# Revit family: Shower-Rainhead-KOHLER-K-26291IN
name_source: partatom
category: Plumbing Fixtures
revit_build: Autodesk Revit 2017 (Build: 20160225_1515(x64)
units: mm (PartAtom-declared; Revit-internal decimal feet)

## family parameters
Cut with Voids When Loaded = No
Host = Face
OmniClass Number = 23.31.17.00
Part Type = Normal
Room Calculation Point = No
Round Connector Dimension = Use Diameter
Shared = No

## types (6) — shared parameters
ADA Compliant = No
Assembly Code = D2010700
CW Connection = No
Cold Water Inlet = Cold Water Inlet
Date Modified = 02/01/2021
Default Elevation = 0"
Description = 10 in Round Katalyst Rainhead 2.5 GPM
Drain Included = No
Flow Rate = 3 GPM
HW Connection = Yes
Height = 4"
Hot Water Inlet = Tempered Water Inlet
Length = 11 15/16"
Manufacturer = KOHLER Co.
Master Format 2014 = 22 42 23
Master Format 2014 Name = Residential Showers
Material = Brass Construction
Pressure = 0.00 psi
URL = https://www.kohler.co.in
Vent Connection = No
Waste Connection = No
Waste Water Outlet = Waste Water Outlet
WaterSense Certified = No
Width = 11 15/16"

## per-type parameters (varying)
| type | Finish | Model | Product Name | Type |
| CP-Polished Chrome | Kohler-Metal-CP-Polished_Chrome | K-26291IN-CP |  | 1 |
| BN-Vibrant Brushed Nickel | Kohler-Metal-BN-Vibrant_Brushed_Nickel | K-26291IN-BN | Rainhead | 4 |
| BL-Matte Black | Kohler-Metal-BL-Matte_Black | K-26291IN-BL | Rainhead | 3 |
| RGD-Rose Gold | Kohler-Metal-RGD-Rose_Gold | K-26291IN-RGD | Rainhead | 6 |
| AF-Flange Gold | Kohler-Metal-AF-Flange_Gold | K-26291IN-AF | Rainhead | 2 |
| BV-Roman Copper | Kohler-Metal-BV-Roman_Copper | K-26291IN-BV | Rainhead | 5 |

## geometry (parser evidence)
native form markers: Sweep x5
no freeform markers — native parametric forms only
